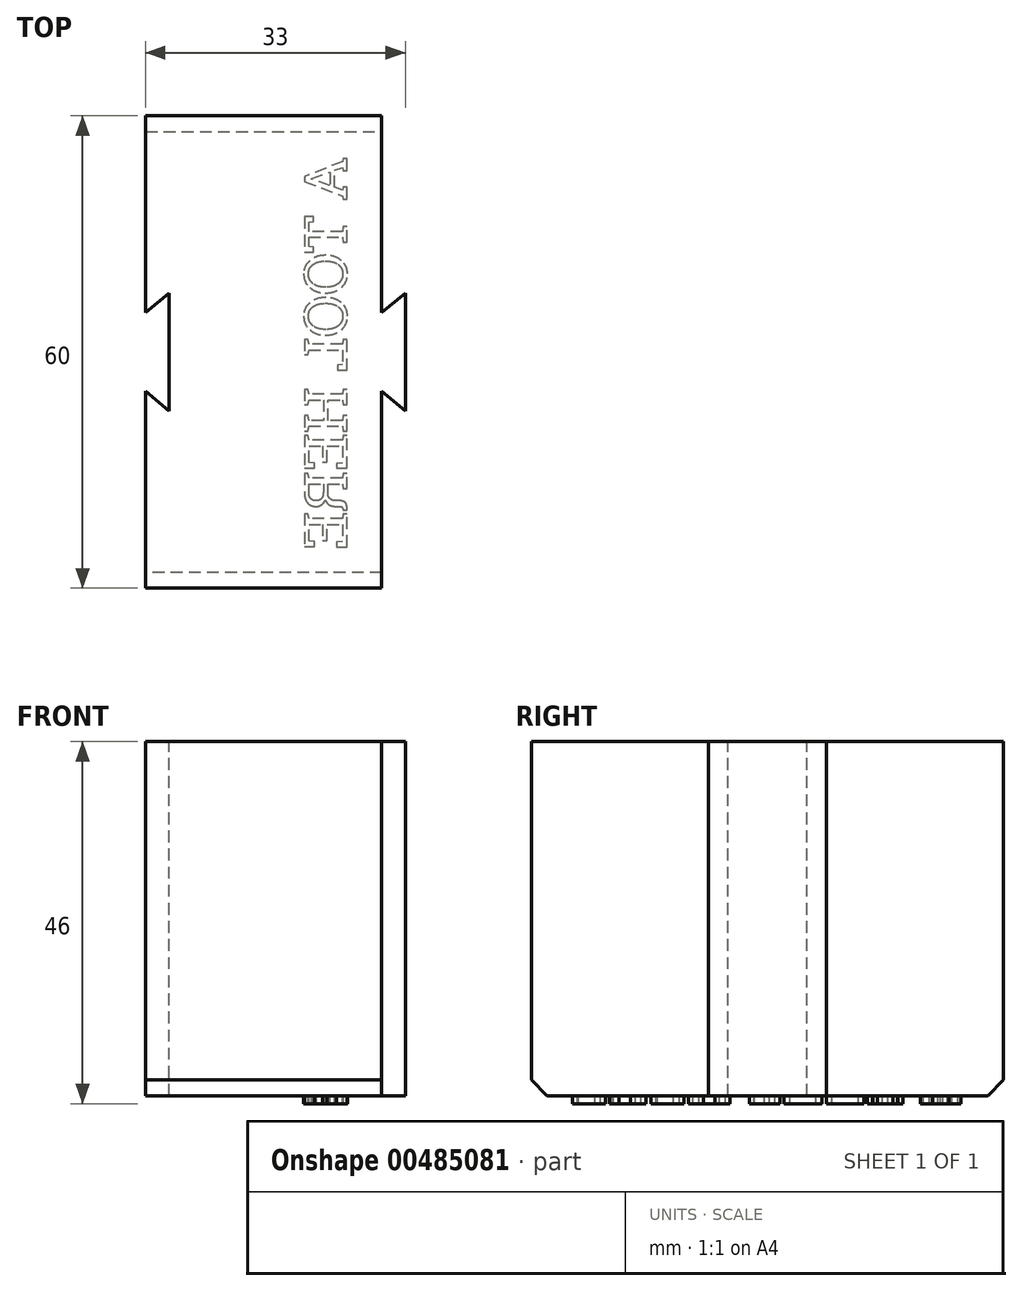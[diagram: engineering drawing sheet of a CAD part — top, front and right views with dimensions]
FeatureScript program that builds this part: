
annotation { "Feature Type Name" : "Feature", "Feature Type Description" : "" }
export const myFeature = defineFeature(function(context is Context, id is Id, definition is map)
    precondition{}
    {
        {
            var Q0;
            Q0=qCreatedBy(makeId("Top.planeOp"),FACE);
            var sketch = newSketch(context, id + "F0", { "sketchPlane" : qUnion([Q0])});
            skPoint(sketch, "E0.middle", {"position": v(0, 0) * mm});
            skLineSegment(sketch, "E1.bottom", {"start": v(15, 30) * mm, "end": v(-15, 30) * mm});
            skLineSegment(sketch, "E1.top", {"start": v(15, -30) * mm, "end": v(-15, -30) * mm});
            skLineSegment(sketch, "E2.left", {"start": v(-12, 7.5) * mm, "end": v(-12, -7.5) * mm});
            skLineSegment(sketch, "E3.left", {"start": v(18, 7.5) * mm, "end": v(18, -7.5) * mm});
            skLineSegment(sketch, "E4", {"start": v(-12, 7.5) * mm, "end": v(-15, 5) * mm});
            skLineSegment(sketch, "E5", {"start": v(15, 30) * mm, "end": v(15, 5) * mm});
            skLineSegment(sketch, "E6", {"start": v(15, -5) * mm, "end": v(15, -30) * mm});
            skLineSegment(sketch, "E7", {"start": v(-15, -30) * mm, "end": v(-15, -5) * mm});
            skLineSegment(sketch, "E8", {"start": v(-12, -7.5) * mm, "end": v(-12, 7.5) * mm});
            skLineSegment(sketch, "E9", {"start": v(-15, -5) * mm, "end": v(-12, -7.5) * mm});
            skLineSegment(sketch, "E10", {"start": v(-15, 5) * mm, "end": v(-15, 30) * mm});
            skLineSegment(sketch, "E11", {"start": v(15, 5) * mm, "end": v(18, 7.5) * mm});
            skLineSegment(sketch, "E12", {"start": v(15, -5) * mm, "end": v(18, -7.5) * mm});
            skSolve(sketch);
        }
        {
            var Q0;
            Q0=makeQuery(id+"F0.imprint","IMPRINT",FACE,{"disambiguationData":[TD([[makeQuery(id+"F0.imprint","IMPRINT",EDGE,{"derivedFrom":sQuery(id+"F0.wireOp",EDGE,"E1.bottom")}),1.0]])]});
            extrude(context, id + "F1", {"entities" : qUnion([Q0]), "oppositeDirection" : true, "depth" : 40 * mm});
        }
        {
            var Q0;
            Q0=makeQuery(id+"F0.imprint","IMPRINT",FACE,{"disambiguationData":[TD([[makeQuery(id+"F0.imprint","IMPRINT",EDGE,{"derivedFrom":sQuery(id+"F0.wireOp",EDGE,"E1.bottom")}),1.0]])]});
            extrude(context, id + "F2", {"entities" : qUnion([Q0]), "operationType" : NewBodyOperationType.ADD, "depth" : 5 * mm});
        }
        {
            var Q0;
            Q0=makeQuery(id+"F1.opExtrude","CAP_EDGE",EDGE,{"disambiguationData":[OSD([sQuery(id+"F0.wireOp",EDGE,"E1.bottom")])],"isStart":false});
            var Q1;
            Q1=makeQuery(id+"F1.opExtrude","CAP_EDGE",EDGE,{"disambiguationData":[OSD([sQuery(id+"F0.wireOp",EDGE,"E1.top")])],"isStart":false});
            chamfer(context, id + "F3", {"entities" : qUnion([Q0, Q1]), "width" : 2 * mm, "tangentPropagation" : true});
        }
        {
            var Q0;
            Q0=makeQuery(id+"F1.opExtrude","CAP_FACE",FACE,{"disambiguationData":[OSD([sQuery(id+"F0.wireOp",EDGE,"E1.bottom"),sQuery(id+"F0.wireOp",EDGE,"E1.top"),sQuery(id+"F0.wireOp",EDGE,"E4"),sQuery(id+"F0.wireOp",EDGE,"E5"),sQuery(id+"F0.wireOp",EDGE,"E3.left"),sQuery(id+"F0.wireOp",EDGE,"E6"),sQuery(id+"F0.wireOp",EDGE,"E7"),sQuery(id+"F0.wireOp",EDGE,"E8"),sQuery(id+"F0.wireOp",EDGE,"E9"),sQuery(id+"F0.wireOp",EDGE,"E10"),sQuery(id+"F0.wireOp",EDGE,"E11"),sQuery(id+"F0.wireOp",EDGE,"E12")])],"isStart":false});
            var sketch = newSketch(context, id + "F4", { "sketchPlane" : qUnion([Q0])});
            skText(sketch, "E13", { "text": "A TOOL HERE", "fontName": "RobotoSlab-Regular.ttf"});
            const initialGuessF4  = {"E13": [0.01057, -0.02478, 0, 1, 0.00547]};
            skSetInitialGuess(sketch, initialGuessF4);
            skSolve(sketch);
        }
        {
            var Q0;
            Q0 = qSketchRegion(id + "F4", true);
            extrude(context, id + "F5", {"entities" : qUnion([Q0]), "operationType" : NewBodyOperationType.ADD, "depth" : 1 * mm});
        }
    });
